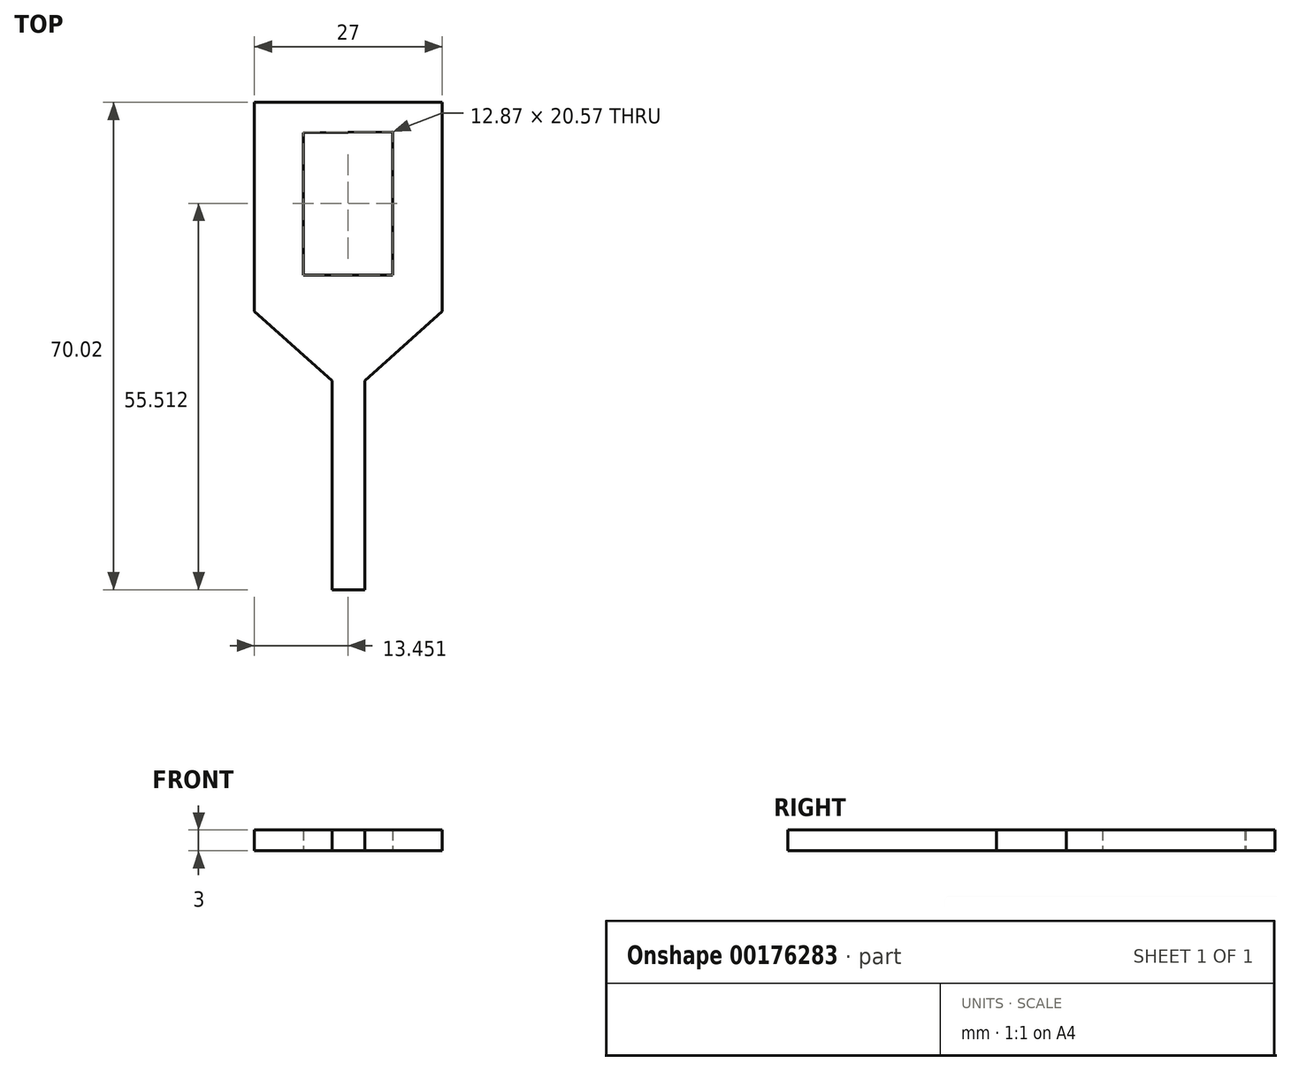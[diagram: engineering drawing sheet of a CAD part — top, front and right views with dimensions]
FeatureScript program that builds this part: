
annotation { "Feature Type Name" : "Feature", "Feature Type Description" : "" }
export const myFeature = defineFeature(function(context is Context, id is Id, definition is map)
    precondition{}
    {
        {
            var Q0;
            Q0=qCreatedBy(makeId("Top.planeOp"),FACE);
            var sketch = newSketch(context, id + "F0", { "sketchPlane" : qUnion([Q0])});
            skLineSegment(sketch, "E0", {"start": v(13.5, 3.34) * mm, "end": v(13.5, -26.66) * mm});
            skLineSegment(sketch, "E1", {"start": v(13.5, -26.66) * mm, "end": v(2.33, -36.68) * mm});
            skLineSegment(sketch, "E2", {"start": v(2.33, -36.68) * mm, "end": v(2.33, -66.68) * mm});
            skLineSegment(sketch, "E3.MirrorCS", {"start": v(-13.5, 3.34) * mm, "end": v(-13.5, -26.66) * mm});
            skLineSegment(sketch, "E4.MirrorCS", {"start": v(-13.5, -26.66) * mm, "end": v(-2.33, -36.68) * mm});
            skLineSegment(sketch, "E5.MirrorCS", {"start": v(-2.33, -36.68) * mm, "end": v(-2.33, -66.68) * mm});
            skLineSegment(sketch, "E6", {"start": v(-13.5, 3.34) * mm, "end": v(13.5, 3.34) * mm});
            skLineSegment(sketch, "E7", {"start": v(-2.33, -66.68) * mm, "end": v(2.33, -66.68) * mm});
            skLineSegment(sketch, "E8", {"start": v(-6.49, -1) * mm, "end": v(-6.49, -21.45) * mm});
            skLineSegment(sketch, "E9", {"start": v(-6.49, -21.45) * mm, "end": v(6.39, -21.45) * mm});
            skLineSegment(sketch, "E10", {"start": v(6.39, -21.45) * mm, "end": v(6.39, -0.88) * mm});
            skLineSegment(sketch, "E11", {"start": v(6.39, -0.88) * mm, "end": v(-6.49, -1) * mm});
            skSolve(sketch);
        }
        {
            var Q0;
            Q0=makeQuery(id+"F0.imprint","IMPRINT",FACE,{"disambiguationData":[TD([[makeQuery(id+"F0.imprint","IMPRINT",EDGE,{"derivedFrom":sQuery(id+"F0.wireOp",EDGE,"E0")}),-1.0]])]});
            extrude(context, id + "F1", {"entities" : qUnion([Q0]), "depth" : 3 * mm});
        }
    });
